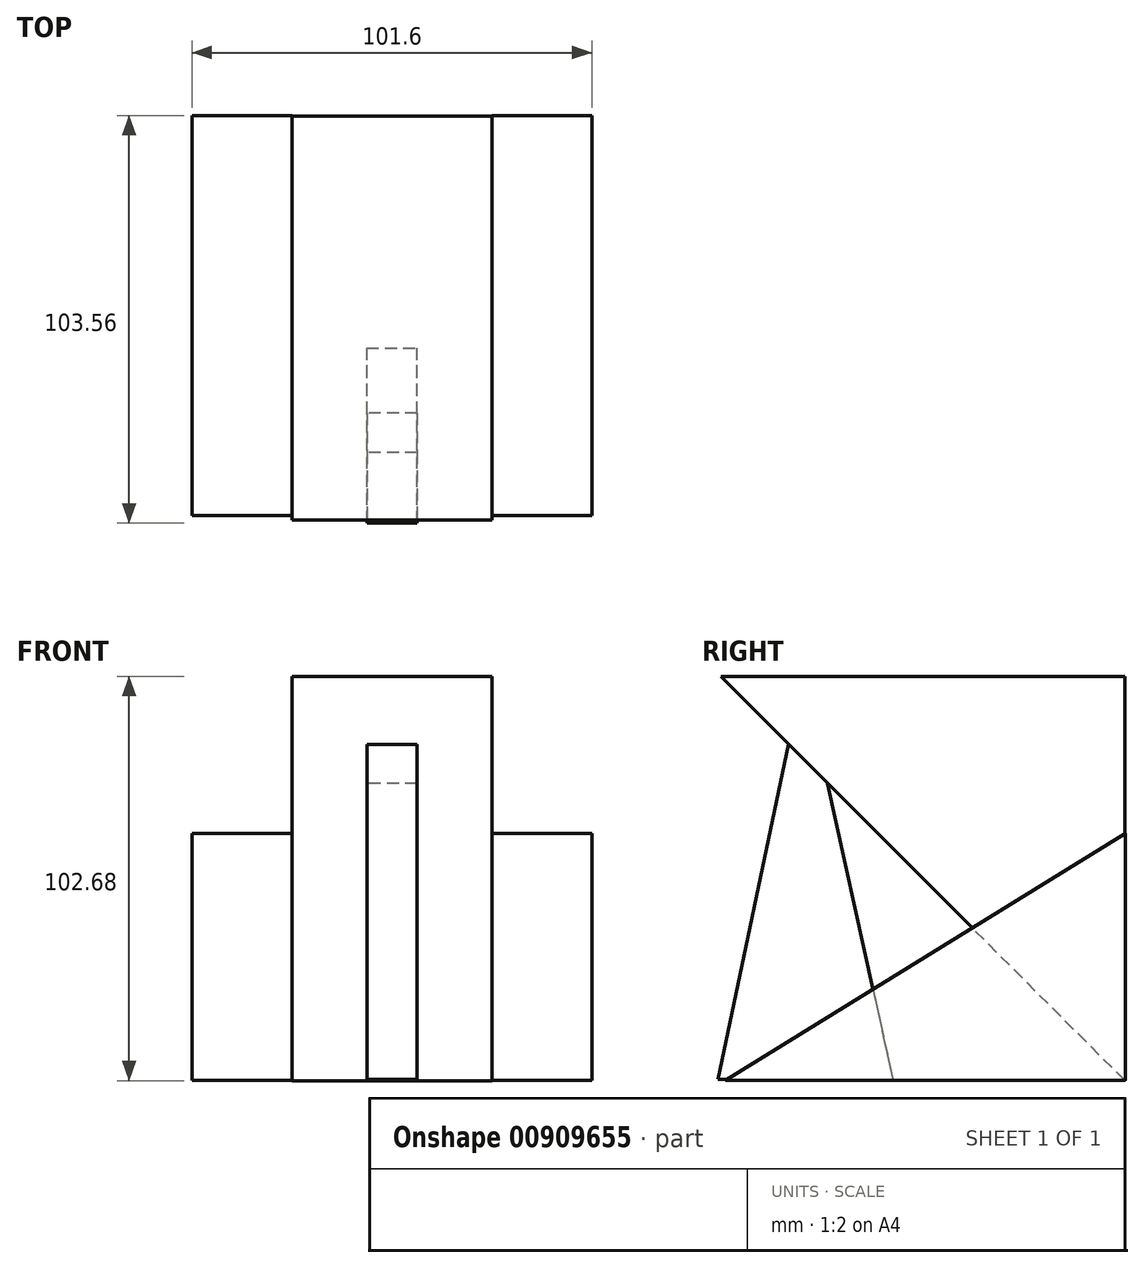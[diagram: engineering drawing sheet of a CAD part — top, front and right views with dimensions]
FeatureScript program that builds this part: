
annotation { "Feature Type Name" : "Feature", "Feature Type Description" : "" }
export const myFeature = defineFeature(function(context is Context, id is Id, definition is map)
    precondition{}
    {
        {
            var Q0;
            Q0=qCreatedBy(makeId("Right.planeOp"),FACE);
            var sketch = newSketch(context, id + "F0", { "sketchPlane" : qUnion([Q0])});
            skLineSegment(sketch, "E0", {"start": v(0, 51.52) * mm, "end": v(-51.43, 51.52) * mm});
            skLineSegment(sketch, "E1.bottom", {"start": v(0, 51.52) * mm, "end": v(51.25, 51.52) * mm});
            skLineSegment(sketch, "E2", {"start": v(51.25, 51.52) * mm, "end": v(51.25, -51.16) * mm});
            skLineSegment(sketch, "E3", {"start": v(51.25, -51.16) * mm, "end": v(-51.43, 51.52) * mm});
            skSolve(sketch);
        }
        {
            var Q0;
            Q0 = qSketchRegion(id + "F0", true);
            extrude(context, id + "F1", {"entities" : qUnion([Q0]), "endBound" : BoundingType.SYMMETRIC, "depth" : 50.8 * mm, "offsetDistance" : 25.4 * mm});
        }
        {
            var Q0;
            Q0=qCreatedBy(makeId("Right.planeOp"),FACE);
            var sketch = newSketch(context, id + "F2", { "sketchPlane" : qUnion([Q0])});
            skLineSegment(sketch, "E4", {"start": v(-26.79, 35.66) * mm, "end": v(-33.14, 39.54) * mm});
            skLineSegment(sketch, "E5", {"start": v(-26.79, 35.66) * mm, "end": v(-7.74, -50.8) * mm});
            skLineSegment(sketch, "E6", {"start": v(-33.14, 39.54) * mm, "end": v(-52.19, -50.8) * mm});
            skLineSegment(sketch, "E7", {"start": v(-52.19, -50.8) * mm, "end": v(-7.74, -50.8) * mm});
            skSolve(sketch);
        }
        {
            var Q0;
            Q0 = qSketchRegion(id + "F2", true);
            extrude(context, id + "F3", {"entities" : qUnion([Q0]), "operationType" : NewBodyOperationType.ADD, "endBound" : BoundingType.SYMMETRIC, "oppositeDirection" : true, "depth" : 12.7 * mm, "offsetDistance" : 25.4 * mm});
        }
        {
            var Q0;
            Q0=qCreatedBy(makeId("Right.planeOp"),FACE);
            var sketch = newSketch(context, id + "F4", { "sketchPlane" : qUnion([Q0])});
            skLineSegment(sketch, "E8", {"start": v(51.37, 0) * mm, "end": v(51.37, -51.09) * mm});
            skLineSegment(sketch, "E9", {"start": v(51.37, -51.09) * mm, "end": v(-50.22, -51.09) * mm});
            skLineSegment(sketch, "E10", {"start": v(51.37, 0) * mm, "end": v(51.37, 12.83) * mm});
            skLineSegment(sketch, "E11", {"start": v(-50.22, -51.09) * mm, "end": v(53.27, 12.83) * mm});
            skSolve(sketch);
        }
        {
            var Q0;
            Q0 = qSketchRegion(id + "F4", true);
            extrude(context, id + "F5", {"entities" : qUnion([Q0]), "depth" : 50.8 * mm, "offsetDistance" : 25.4 * mm, "hasSecondDirection" : true, "secondDirectionOppositeDirection" : false, "secondDirectionDepth" : 25.4 * mm});
        }
        {
            var Q0;
            Q0 = qSketchRegion(id + "F4", true);
            extrude(context, id + "F6", {"entities" : qUnion([Q0]), "operationType" : NewBodyOperationType.ADD, "oppositeDirection" : true, "depth" : 50.8 * mm, "offsetDistance" : 25.4 * mm, "hasSecondDirection" : true, "secondDirectionOppositeDirection" : true, "secondDirectionDepth" : 25.4 * mm});
        }
    });
